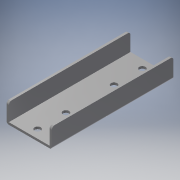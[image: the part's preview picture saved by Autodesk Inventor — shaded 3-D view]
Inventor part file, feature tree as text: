
AUTODESK INVENTOR PART (.ipt)
format: ipt  version: 2017 (Build 210142000, 142)  size: 202,752 bytes
history: native  units: mm
features: other x6, sheet_metal_op x5, sketch x4, plane x2, mirror x1, chamfer x1
ambient origin geometry x8: Origin, YZ Plane, XZ Plane, XY Plane, X Axis, Y Axis, Z Axis, Center Point
bodies: Solid1 (feature_tree)
feature tree (19):
  sheet_metal_op  "Face1"
  sheet_metal_op  "Flange1"
  sheet_metal_op  "Flange2"
  plane  "Work Plane1"
  mirror  "Mirror1"
  chamfer  "Corner Round1"
  plane  "Work Plane2"
  sketch  "Sketch1"  dims[d2=72.0mm]
  other  "Plate1"
  sketch  "Sketch2"  dims[d3=215.0mm]
  other  "Plate2"
  sheet_metal_op  "Bend1"
  sketch  "Sketch3"  dims[d4=0.001mm]
  other  "Plate3"
  sheet_metal_op  "Bend2"
  sketch  "Sketch4"  dims[d5=4.0mm d6=0.001mm d7=8.0mm d8=0.001mm d9=31.0mm d10=90.0deg d11=0.001mm d12=4.0mm d13=0.001mm d14=8.0mm d15=0.001mm d16=31.0mm d17=90.0deg d18=0.001mm d19=11.0mm d20=11.0mm d21=15.0mm d22=50.0mm d23=4.0mm d24=0.0mm d25=5.0mm d0=4.0mm]
  other  "FlatPattern"
  other  "Cut1"
  other  "FlatPatternExtrusion2"
